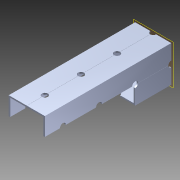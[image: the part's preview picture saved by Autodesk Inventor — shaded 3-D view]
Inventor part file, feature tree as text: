
AUTODESK INVENTOR PART (.ipt)
format: ipt  version: 2014 (Build 180170000, 170)  size: 1,198,080 bytes
history: native  units: in
note: dims shown in document units (in); Inventor stores cm internally (conversion verified against a paired STEP export)
features: extrude x2, pattern_circular x1, other x1, plane x1, imported_body x1, sketch x1
ambient origin geometry x8: Origin, YZ Plane, XZ Plane, XY Plane, X Axis, Y Axis, Z Axis, Center Point
bodies: Body1 (feature_tree)
feature tree (7):
  pattern_circular  "CirPattern2"
  other  "217-3426-STEP1"
  plane  "Work Plane1"
  extrude  "Extrusion1"  Depth=3937.0079in TaperAngle=0.0deg
  extrude  "Extrusion3"  Depth=3.937in TaperAngle=0.0deg
  imported_body  "Base1"
  sketch  "Sketch1"  dims[d0=-3.5in d1=3937.0079in d2=0.0in d5=3.937in d6=0.0in]
